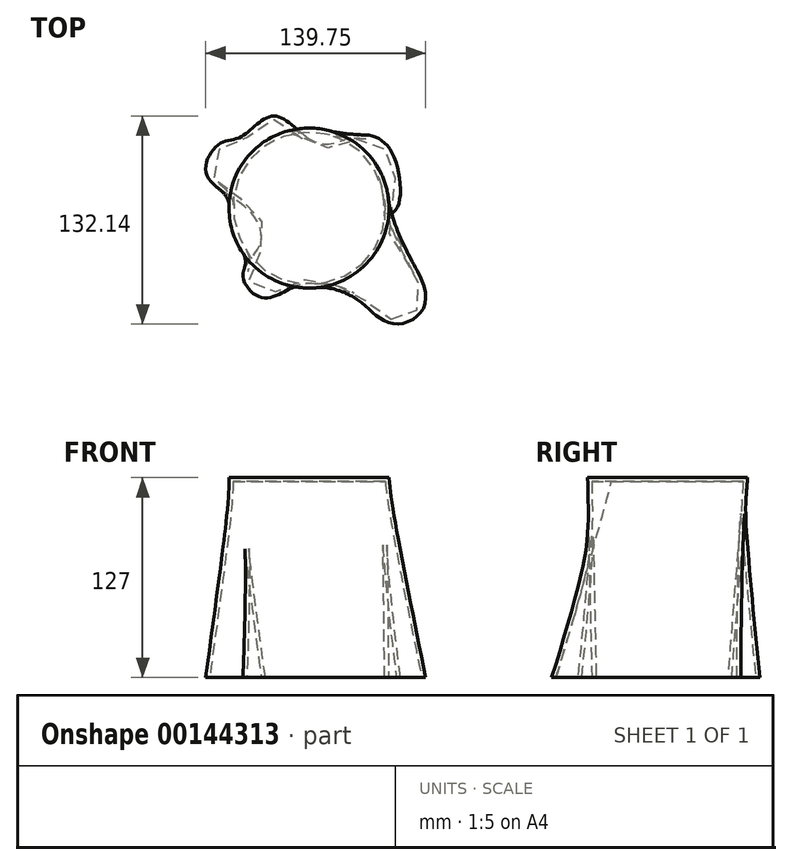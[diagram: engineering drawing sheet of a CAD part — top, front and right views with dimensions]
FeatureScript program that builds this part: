
annotation { "Feature Type Name" : "Feature", "Feature Type Description" : "" }
export const myFeature = defineFeature(function(context is Context, id is Id, definition is map)
    precondition{}
    {
        {
            var Q0;
            Q0=qCreatedBy(makeId("Top.planeOp"),FACE);
            var sketch = newSketch(context, id + "F0", { "sketchPlane" : qUnion([Q0])});
            skFitSpline(sketch, "E0", {"points": [v(-42.83, 45.45) * mm, v(-22.05, 58.48) * mm, v(4.62, 41.73) * mm, v(26.34, 44.83) * mm, v(41.53, 45.45) * mm, v(54.56, 31.19) * mm, v(55.8, 0) * mm, v(50.53, -6.96) * mm, v(71.31, -45.11) * mm, v(71, -66.2) * mm, v(55.8, -73.65) * mm, v(42.15, -67.76) * mm, v(28.82, -56.9) * mm, v(0, -47.9) * mm, v(-15.23, -52.87) * mm, v(-30.73, -56.6) * mm, v(-41.9, -42.01) * mm, v(-31.05, -22.78) * mm, v(-39.73, 0) * mm, v(-65.16, 21.88) * mm, v(-56.79, 40.8) * mm, v(-42.83, 45.45) * mm]});
            skSolve(sketch);
        }
        {
            var Q0;
            Q0=qCreatedBy(makeId("Top.planeOp"),FACE);
            cPlane(context, id + "F1", {"entities" : qUnion([Q0]), "cplaneType" : CPlaneType.OFFSET, "offset" : 127 * mm, "width" : 152.4 * mm, "height" : 152.4 * mm});
        }
        {
            var Q0;
            Q0=qCreatedBy(id+"F1.planeOp",FACE);
            var sketch = newSketch(context, id + "F2", { "sketchPlane" : qUnion([Q0])});
            skCircle(sketch, "E1", {"center": v(0, 0) * mm, "radius": 50.8 * mm});
            skSolve(sketch);
        }
        {
            var Q0;
            Q0=makeQuery(id+"F0.imprint","IMPRINT",FACE,{"disambiguationData":[TD([[makeQuery(id+"F0.imprint","IMPRINT",EDGE,{"derivedFrom":sQuery(id+"F0.wireOp",EDGE,"E0")}),-1.0]])]});
            var Q1;
            Q1=makeQuery(id+"F2.imprint","IMPRINT",FACE,{"disambiguationData":[TD([[makeQuery(id+"F2.imprint","IMPRINT",EDGE,{"derivedFrom":sQuery(id+"F2.wireOp",EDGE,"E1")}),1.0]])]});
            loft(context, id + "F3", {"sheetProfilesArray" : [{ "sheetProfileEntities" : qUnion([Q0]) }, { "sheetProfileEntities" : qUnion([Q1]) }]});
        }
        {
            var Q0;
            Q0=makeQuery(id+"F3.opLoft","CAP_FACE",FACE,{"disambiguationData":[OSD([makeQuery(id+"F0.imprint","IMPRINT",FACE,{"disambiguationData":[TD([[makeQuery(id+"F0.imprint","IMPRINT",EDGE,{"derivedFrom":sQuery(id+"F0.wireOp",EDGE,"E0")}),-1.0]])]})])],"isStart":true});
            shell(context, id + "F4", {"entities" : qUnion([Q0]), "thickness" : 2.54 * mm});
        }
    });
